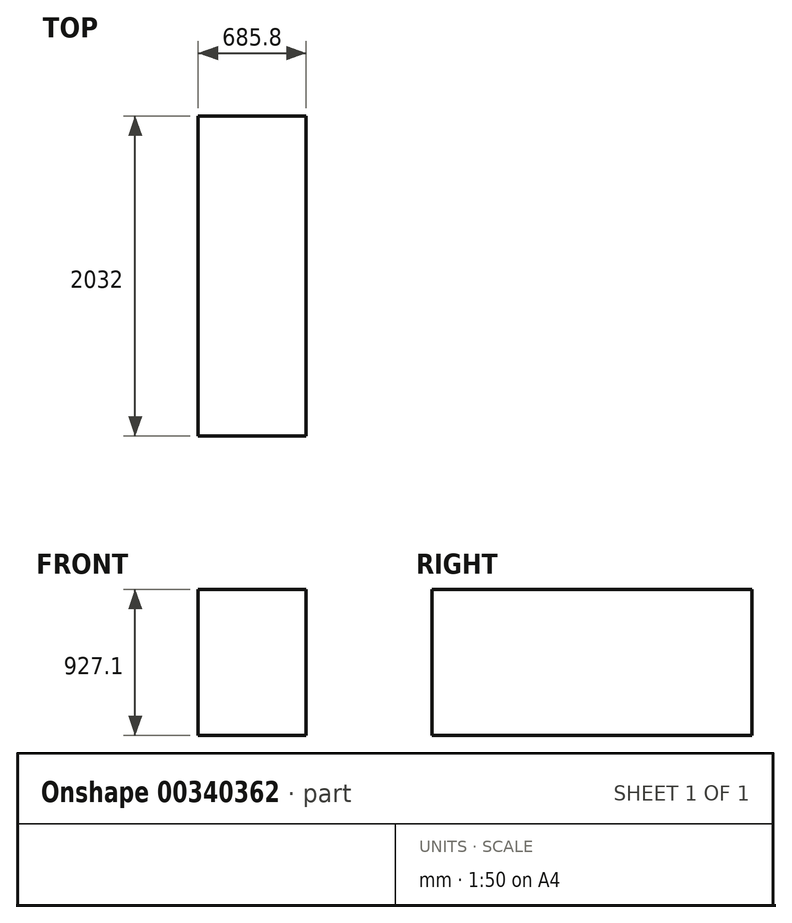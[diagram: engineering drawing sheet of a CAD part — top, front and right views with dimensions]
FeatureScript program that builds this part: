
annotation { "Feature Type Name" : "Feature", "Feature Type Description" : "" }
export const myFeature = defineFeature(function(context is Context, id is Id, definition is map)
    precondition{}
    {
        {
            var Q0;
            Q0=qCreatedBy(makeId("Front.planeOp"),FACE);
            var sketch = newSketch(context, id + "F0", { "sketchPlane" : qUnion([Q0])});
            skLineSegment(sketch, "E0.bottom", {"start": v(342.9, 463.55) * mm, "end": v(-342.9, 463.55) * mm});
            skLineSegment(sketch, "E0.top", {"start": v(342.9, -463.55) * mm, "end": v(-342.9, -463.55) * mm});
            skLineSegment(sketch, "E0.left", {"start": v(342.9, 463.55) * mm, "end": v(342.9, -463.55) * mm});
            skLineSegment(sketch, "E0.right", {"start": v(-342.9, 463.55) * mm, "end": v(-342.9, -463.55) * mm});
            skPoint(sketch, "E0.middle", {"position": v(0, 0) * mm});
            skSolve(sketch);
        }
        {
            var Q0;
            Q0=makeQuery(id+"F0.imprint","IMPRINT",FACE,{"disambiguationData":[TD([[makeQuery(id+"F0.imprint","IMPRINT",EDGE,{"derivedFrom":sQuery(id+"F0.wireOp",EDGE,"E0.bottom")}),1.0]])]});
            extrude(context, id + "F1", {"entities" : qUnion([Q0]), "oppositeDirection" : true, "depth" : 2032 * mm});
        }
    });
